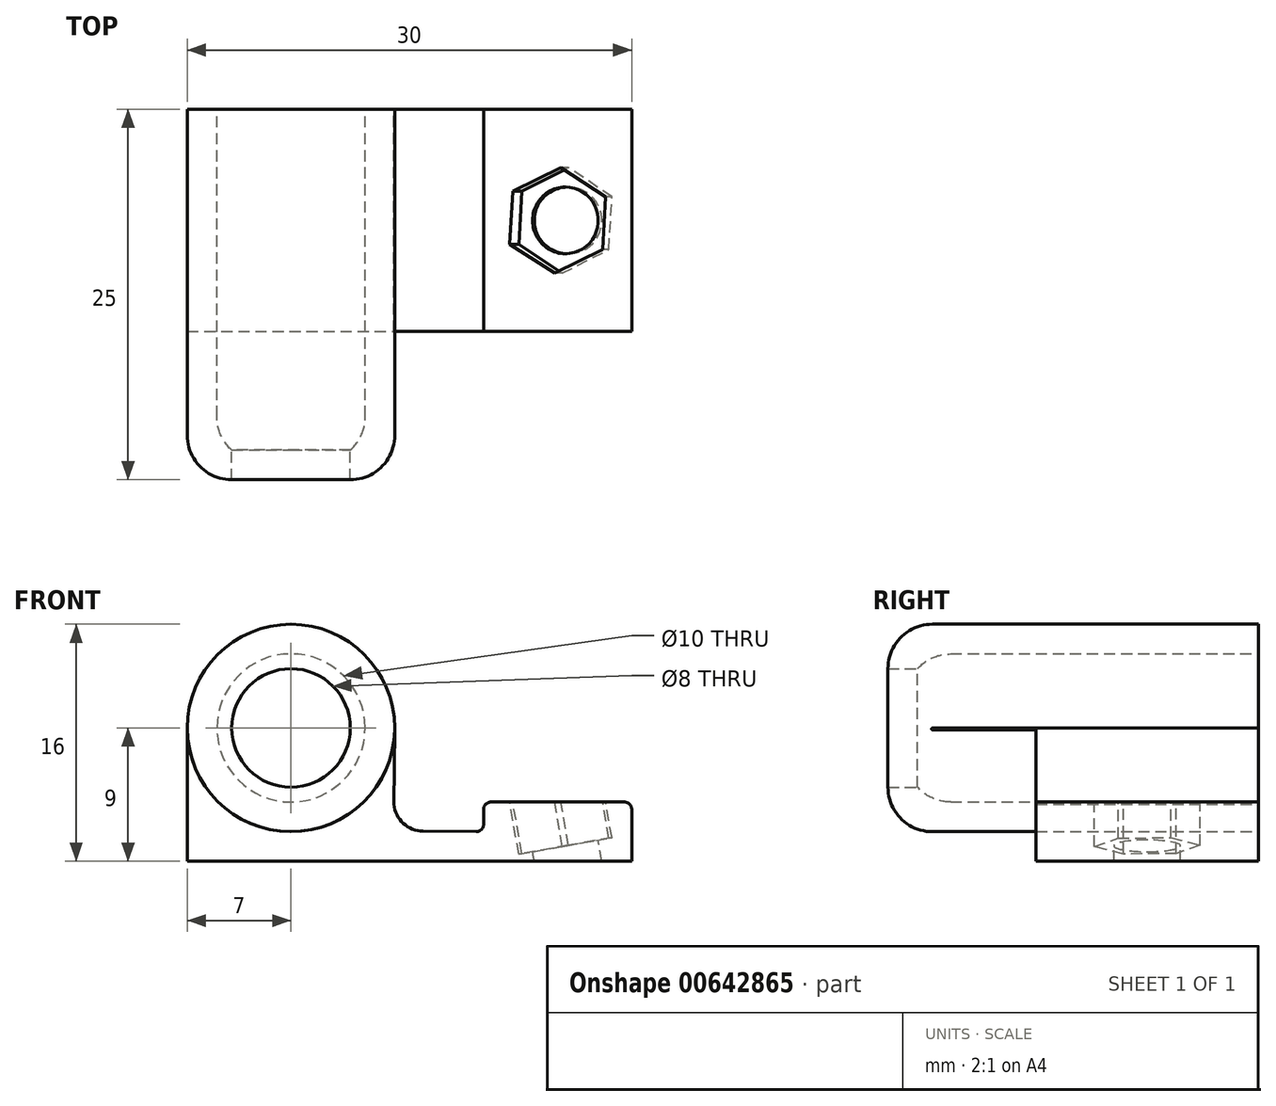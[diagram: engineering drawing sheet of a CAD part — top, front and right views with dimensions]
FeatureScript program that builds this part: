
annotation { "Feature Type Name" : "Feature", "Feature Type Description" : "" }
export const myFeature = defineFeature(function(context is Context, id is Id, definition is map)
    precondition{}
    {
        {
            var Q0;
            Q0=qCreatedBy(makeId("Front.planeOp"),FACE);
            var sketch = newSketch(context, id + "F0", { "sketchPlane" : qUnion([Q0])});
            skLineSegment(sketch, "E0", {"start": v(0, 0) * mm, "end": v(30, 0) * mm});
            skLineSegment(sketch, "E1", {"start": v(30, 0) * mm, "end": v(30, 3.5) * mm});
            skLineSegment(sketch, "E2", {"start": v(20, 3.5) * mm, "end": v(20, 2.5) * mm});
            skLineSegment(sketch, "E3", {"start": v(19.5, 2) * mm, "end": v(15.92, 2.03) * mm});
            skLineSegment(sketch, "E4", {"start": v(0, 8.95) * mm, "end": v(0, 0) * mm});
            skLineSegment(sketch, "E5", {"start": v(20.5, 4) * mm, "end": v(29.5, 4) * mm});
            skPoint(sketch, "E6.endSnap0", {"position": v(7, 4) * mm});
            skCircle(sketch, "E7", {"center": v(7, 9) * mm, "radius": 5 * mm});
            skCircle(sketch, "E8.0", {"center": v(7, 9) * mm, "radius": 7 * mm});
            skPoint(sketch, "E9.visualSharp", {"position": v(-239.5, 4) * mm});
            skArc(sketch, "E9.filletArc", {"start": v(13.95, 3.85) * mm, "mid": v(14.59, 2.56) * mm, "end": v(15.92, 2.03) * mm});
            skLineSegment(sketch, "E10", {"start": v(14, 9) * mm, "end": v(13.95, 3.85) * mm});
            skPoint(sketch, "E11.visualSharp", {"position": v(20, 4) * mm});
            skArc(sketch, "E11.filletArc", {"start": v(20.5, 4) * mm, "mid": v(20.15, 3.85) * mm, "end": v(20, 3.5) * mm});
            skPoint(sketch, "E12.visualSharp", {"position": v(30, 4) * mm});
            skArc(sketch, "E12.filletArc", {"start": v(30, 3.5) * mm, "mid": v(29.85, 3.85) * mm, "end": v(29.5, 4) * mm});
            skPoint(sketch, "E13.visualSharp", {"position": v(20, 2) * mm});
            skArc(sketch, "E13.filletArc", {"start": v(19.5, 2) * mm, "mid": v(19.85, 2.15) * mm, "end": v(20, 2.5) * mm});
            skSolve(sketch);
        }
        {
            var Q0;
            Q0=makeQuery(id+"F0.imprint","IMPRINT",FACE,{"disambiguationData":[TD([[makeQuery(id+"F0.imprint","IMPRINT",EDGE,{"derivedFrom":sQuery(id+"F0.wireOp",EDGE,"E7")}),-1.0]])]});
            var Q1;
            Q1=makeQuery(id+"F0.imprint","IMPRINT",FACE,{"disambiguationData":[TD([[makeQuery(id+"F0.imprint","IMPRINT",EDGE,{"derivedFrom":sQuery(id+"F0.wireOp",EDGE,"E0")}),1.0]])]});
            extrude(context, id + "F1", {"entities" : qUnion([Q0, Q1]), "depth" : 15 * mm, "offsetDistance" : 25 * mm});
        }
        {
            var Q0;
            Q0=makeQuery(id+"F1.opExtrude","SWEPT_FACE",FACE,{"disambiguationData":[OSD([sQuery(id+"F0.wireOp",EDGE,"E5")])]});
            var sketch = newSketch(context, id + "F2", { "sketchPlane" : qUnion([Q0])});
            skLineSegment(sketch, "E14", {"start": v(25, -15) * mm, "end": v(25, 0) * mm, "construction": true});
            skSolve(sketch);
        }
        {
            var Q0;
            {var subQ0=sQuery(id+"F0.wireOp",EDGE,"E5");Q0=makeQuery(id+"F2.imprint","IMPRINT",FACE,{"disambiguationData":[TD([[makeQuery(id+"F2.imprint","IMPRINT",EDGE,{"derivedFrom":makeQuery(id+"F1.opExtrude","CAP_EDGE",EDGE,{"disambiguationData":[OSD([subQ0])],"isStart":true})}),-1.0]])]});}
            var Q1;
            Q1=sQuery(id+"F2.wireOp",EDGE,"E14");
            cPlane(context, id + "F3", {"entities" : qUnion([Q0, Q1]), "cplaneType" : CPlaneType.LINE_ANGLE, "offset" : 25 * mm, "angle" : 10 * degree, "oppositeDirection" : true, "width" : 150 * mm, "height" : 150 * mm});
        }
        {
            var Q0;
            Q0=qCreatedBy(id+"F3.planeOp",FACE);
            var sketch = newSketch(context, id + "F4", { "sketchPlane" : qUnion([Q0])});
            skLineSegment(sketch, "E15.0.0", {"start": v(29.75, 0) * mm, "end": v(20.88, 0) * mm});
            skLineSegment(sketch, "E15.0.1", {"start": v(20.88, 0) * mm, "end": v(20.88, 15) * mm});
            skLineSegment(sketch, "E15.0.2", {"start": v(20.88, 15) * mm, "end": v(29.75, 15) * mm});
            skLineSegment(sketch, "E15.0.3", {"start": v(29.75, 15) * mm, "end": v(29.75, 0) * mm});
            skLineSegment(sketch, "E16", {"start": v(20.88, 7.5) * mm, "end": v(29.75, 7.5) * mm, "construction": true});
            skCircle(sketch, "E17", {"center": v(25.31, 7.5) * mm, "radius": 2.25 * mm});
            skCircle(sketch, "E18.cCircle", {"center": v(25.31, 7.5) * mm, "radius": 3.1 * mm, "construction": true});
            skLineSegment(sketch, "E18.0", {"start": v(25.1, 11.06) * mm, "end": v(28.3, 9.46) * mm});
            skLineSegment(sketch, "E18.1", {"start": v(28.3, 9.46) * mm, "end": v(28.5, 5.9) * mm});
            skLineSegment(sketch, "E18.2", {"start": v(28.5, 5.9) * mm, "end": v(25.52, 3.94) * mm});
            skLineSegment(sketch, "E18.3", {"start": v(25.52, 3.94) * mm, "end": v(22.33, 5.54) * mm});
            skLineSegment(sketch, "E18.4", {"start": v(22.33, 5.54) * mm, "end": v(22.13, 9.1) * mm});
            skLineSegment(sketch, "E18.5", {"start": v(22.13, 9.1) * mm, "end": v(25.1, 11.06) * mm});
            skPoint(sketch, "E18.0.midPoint", {"position": v(26.7, 10.26) * mm});
            skSolve(sketch);
        }
        {
            var Q0;
            Q0=makeQuery(id+"F4.imprint","IMPRINT",FACE,{"disambiguationData":[TD([[makeQuery(id+"F4.imprint","IMPRINT",EDGE,{"derivedFrom":sQuery(id+"F4.wireOp",EDGE,"E17")}),1.0]])]});
            extrude(context, id + "F5", {"entities" : qUnion([Q0]), "operationType" : NewBodyOperationType.REMOVE, "endBound" : BoundingType.THROUGH_ALL, "depth" : 25 * mm, "offsetDistance" : 25 * mm, "hasSecondDirection" : true, "secondDirectionBound" : SecondDirectionBoundingType.THROUGH_ALL, "secondDirectionOppositeDirection" : true, "secondDirectionDepth" : 25 * mm});
        }
        {
            var Q0;
            Q0=makeQuery(id+"F4.imprint","IMPRINT",FACE,{"disambiguationData":[TD([[makeQuery(id+"F4.imprint","IMPRINT",EDGE,{"derivedFrom":sQuery(id+"F4.wireOp",EDGE,"E17")}),-1.0]])]});
            extrude(context, id + "F6", {"entities" : qUnion([Q0]), "operationType" : NewBodyOperationType.REMOVE, "depth" : 3 * mm, "offsetDistance" : 25 * mm, "hasSecondDirection" : true, "secondDirectionBound" : SecondDirectionBoundingType.THROUGH_ALL, "secondDirectionOppositeDirection" : true, "secondDirectionDepth" : 25 * mm});
        }
        {
            var Q0;
            Q0=makeQuery(id+"F1.opExtrude","CAP_FACE",FACE,{"disambiguationData":[OSD([sQuery(id+"F0.wireOp",EDGE,"E0"),sQuery(id+"F0.wireOp",EDGE,"E1"),sQuery(id+"F0.wireOp",EDGE,"E2"),sQuery(id+"F0.wireOp",EDGE,"E3"),sQuery(id+"F0.wireOp",EDGE,"E4"),sQuery(id+"F0.wireOp",EDGE,"E5"),sQuery(id+"F0.wireOp",EDGE,"E7"),sQuery(id+"F0.wireOp",EDGE,"E8.0"),sQuery(id+"F0.wireOp",EDGE,"E9.filletArc"),sQuery(id+"F0.wireOp",EDGE,"E10"),sQuery(id+"F0.wireOp",EDGE,"E11.filletArc"),sQuery(id+"F0.wireOp",EDGE,"E12.filletArc"),sQuery(id+"F0.wireOp",EDGE,"E13.filletArc")])],"isStart":false});
            var sketch = newSketch(context, id + "F7", { "sketchPlane" : qUnion([Q0])});
            skCircle(sketch, "E19.0", {"center": v(7, 9) * mm, "radius": 5 * mm});
            skArc(sketch, "E20.0", {"start": v(14, 8.86) * mm, "mid": v(7.05, 16) * mm, "end": v(0, 8.95) * mm});
            skCircle(sketch, "E21", {"center": v(7, 9) * mm, "radius": 7 * mm});
            skCircle(sketch, "E22.0", {"center": v(7, 9) * mm, "radius": 4 * mm});
            skSolve(sketch);
        }
        {
            var Q0;
            Q0=makeQuery(id+"F7.imprint","IMPRINT",FACE,{"disambiguationData":[TD([[makeQuery(id+"F7.imprint","IMPRINT",EDGE,{"derivedFrom":sQuery(id+"F7.wireOp",EDGE,"E19.0")}),-1.0]])]});
            var Q1;
            Q1=makeQuery(id+"F7.imprint","IMPRINT",FACE,{"disambiguationData":[TD([[makeQuery(id+"F7.imprint","IMPRINT",EDGE,{"derivedFrom":sQuery(id+"F7.wireOp",EDGE,"E19.0")}),1.0]])]});
            extrude(context, id + "F8", {"entities" : qUnion([Q0, Q1]), "operationType" : NewBodyOperationType.ADD, "depth" : 10 * mm, "offsetDistance" : 25 * mm});
        }
        {
            var Q0;
            Q0=makeQuery(id+"F8.opExtrude","CAP_FACE",FACE,{"disambiguationData":[OSD([sQuery(id+"F7.wireOp",EDGE,"E21"),sQuery(id+"F7.wireOp",EDGE,"E22.0")])],"isStart":true});
            var Q1;
            Q1=makeQuery(id+"F8.opExtrude","CAP_FACE",FACE,{"disambiguationData":[OSD([sQuery(id+"F7.wireOp",EDGE,"E21"),sQuery(id+"F7.wireOp",EDGE,"E22.0")])],"isStart":false});
            extrude(context, id + "F9", {"entities" : qUnion([Q0]), "operationType" : NewBodyOperationType.REMOVE, "endBound" : BoundingType.UP_TO_SURFACE, "oppositeDirection" : true, "depth" : 25 * mm, "endBoundEntityFace" : qUnion([Q1]), "hasOffset" : true, "offsetDistance" : 2 * mm});
        }
        {
            var Q0;
            Q0=makeQuery(id+"F8.opExtrude","CAP_EDGE",EDGE,{"disambiguationData":[OSD([sQuery(id+"F7.wireOp",EDGE,"E21")])],"isStart":false});
            fillet(context, id + "F10", {"entities" : qUnion([Q0]), "radius" : 3 * mm, "tangentPropagation" : true, "allowEdgeOverflow" : false});
        }
        {
            var Q0;
            Q0=makeQuery(id+"F9.boolean.opBoolean","COPY",EDGE,{"derivedFrom":makeQuery(id+"F9.opExtrude","CAP_EDGE",EDGE,{"disambiguationData":[OSD([sQuery(id+"F0.wireOp",EDGE,"E7")])],"isStart":false})});
            fillet(context, id + "F11", {"entities" : qUnion([Q0]), "radius" : 3 * mm, "tangentPropagation" : true, "allowEdgeOverflow" : false});
        }
    });
